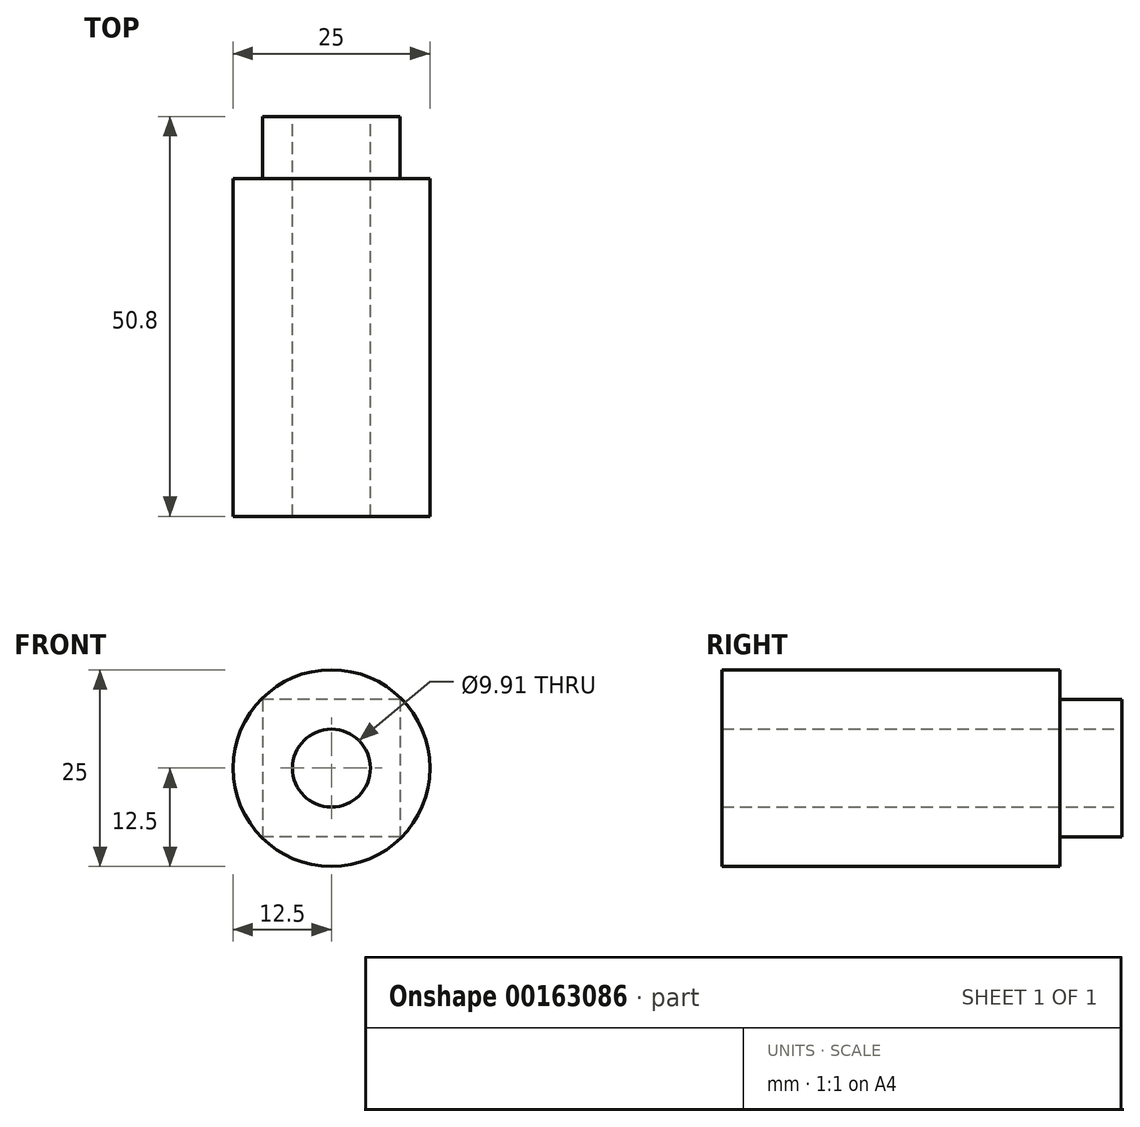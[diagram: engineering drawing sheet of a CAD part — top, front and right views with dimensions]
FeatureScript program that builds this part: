
annotation { "Feature Type Name" : "Feature", "Feature Type Description" : "" }
export const myFeature = defineFeature(function(context is Context, id is Id, definition is map)
    precondition{}
    {
        {
            var Q0;
            Q0=qCreatedBy(makeId("Front.planeOp"),FACE);
            var sketch = newSketch(context, id + "F0", { "sketchPlane" : qUnion([Q0])});
            skCircle(sketch, "E0", {"center": v(0, 0) * mm, "radius": 12.5 * mm});
            skSolve(sketch);
        }
        {
            var Q0;
            Q0=qCreatedBy(makeId("Front.planeOp"),FACE);
            var sketch = newSketch(context, id + "F1", { "sketchPlane" : qUnion([Q0])});
            skLineSegment(sketch, "E1.bottom", {"start": v(8.72, 8.72) * mm, "end": v(-8.72, 8.72) * mm});
            skLineSegment(sketch, "E1.top", {"start": v(8.72, -8.72) * mm, "end": v(-8.72, -8.72) * mm});
            skLineSegment(sketch, "E1.left", {"start": v(8.72, 8.72) * mm, "end": v(8.72, -8.72) * mm});
            skLineSegment(sketch, "E1.right", {"start": v(-8.72, 8.72) * mm, "end": v(-8.72, -8.72) * mm});
            skPoint(sketch, "E1.middle", {"position": v(0, 0) * mm});
            skSolve(sketch);
        }
        {
            var Q0;
            Q0 = qSketchRegion(id + "F0", true);
            extrude(context, id + "F2", {"entities" : qUnion([Q0]), "depth" : 42.9 * mm});
        }
        {
            var Q0;
            Q0 = qSketchRegion(id + "F1", true);
            extrude(context, id + "F3", {"entities" : qUnion([Q0]), "operationType" : NewBodyOperationType.ADD, "oppositeDirection" : true, "depth" : 7.9 * mm});
        }
        {
            var Q0;
            Q0=makeQuery(id+"F3.opExtrude","CAP_FACE",FACE,{"disambiguationData":[OSD([sQuery(id+"F1.wireOp",EDGE,"E1.bottom"),sQuery(id+"F1.wireOp",EDGE,"E1.top"),sQuery(id+"F1.wireOp",EDGE,"E1.left"),sQuery(id+"F1.wireOp",EDGE,"E1.right")])],"isStart":false});
            var sketch = newSketch(context, id + "F4", { "sketchPlane" : qUnion([Q0])});
            skCircle(sketch, "E2", {"center": v(0, 0) * mm, "radius": 4.95 * mm});
            skSolve(sketch);
        }
        {
            var Q0;
            Q0 = qSketchRegion(id + "F4", true);
            extrude(context, id + "F5", {"entities" : qUnion([Q0]), "operationType" : NewBodyOperationType.REMOVE, "oppositeDirection" : true, "depth" : 76.2 * mm});
        }
    });
